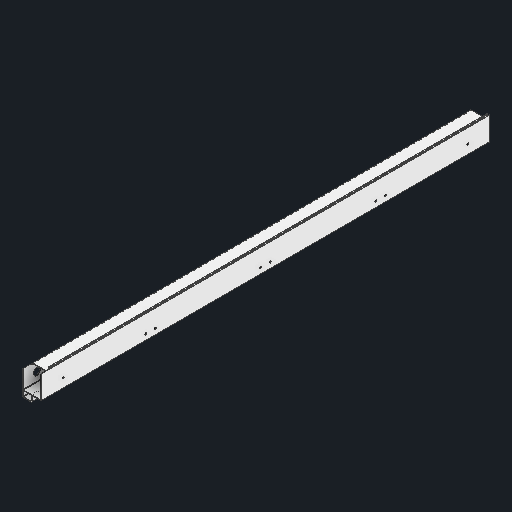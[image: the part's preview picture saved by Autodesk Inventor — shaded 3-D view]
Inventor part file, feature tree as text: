
AUTODESK INVENTOR PART (.ipt)
format: ipt  version: 2025 (Build 290162000, 162)  size: 154,112 bytes
history: native  units: in
note: dims shown in document units (in); Inventor stores cm internally (conversion verified against a paired STEP export)
features: fillet x1
ambient origin geometry x8: Origin, YZ Plane, XZ Plane, XY Plane, X Axis, Y Axis, Z Axis, Center Point
bodies: Solid1 (feature_tree)
feature tree (1):
  fillet  "Fillet6"  [1 undecoded]
note: 1 required parameter value undecoded (feature->parameter linkage not recoverable at this tier; creation-order binding heuristic only, values carry confidence <= 0.55)
